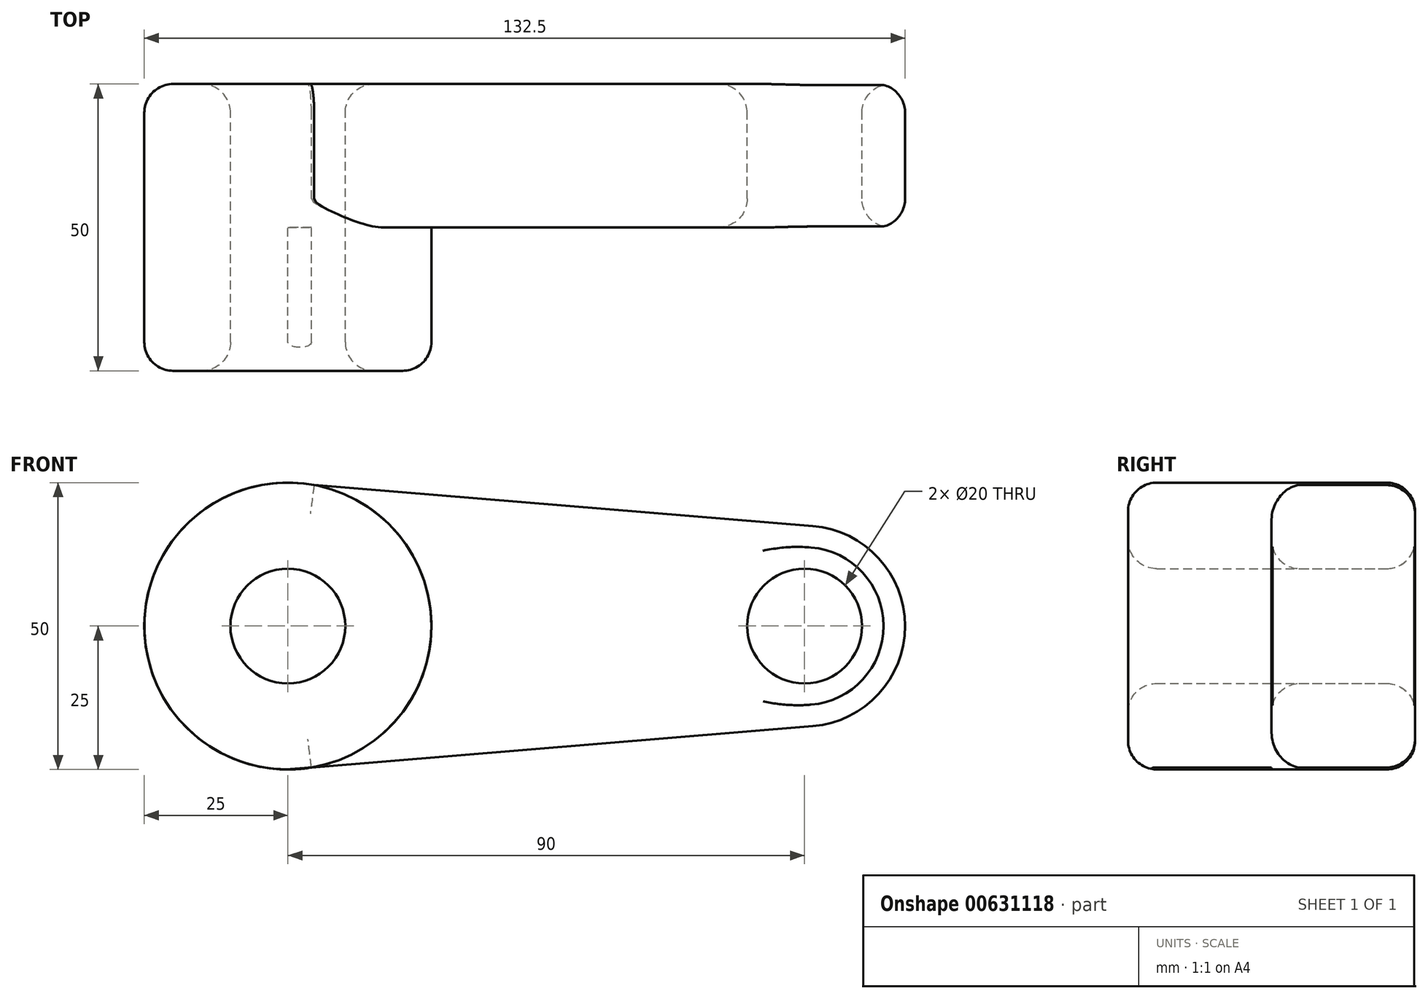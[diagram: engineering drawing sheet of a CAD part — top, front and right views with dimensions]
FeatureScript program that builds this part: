
annotation { "Feature Type Name" : "Feature", "Feature Type Description" : "" }
export const myFeature = defineFeature(function(context is Context, id is Id, definition is map)
    precondition{}
    {
        {
            var Q0;
            Q0=qCreatedBy(makeId("Front.planeOp"),FACE);
            var sketch = newSketch(context, id + "F0", { "sketchPlane" : qUnion([Q0])});
            skCircle(sketch, "E0", {"center": v(0, 0) * mm, "radius": 25 * mm});
            skCircle(sketch, "E1", {"center": v(90, 0) * mm, "radius": 17.5 * mm});
            skLineSegment(sketch, "E2", {"start": v(4.58, 24.58) * mm, "end": v(91.43, 17.44) * mm});
            skLineSegment(sketch, "E3", {"start": v(0, -25) * mm, "end": v(91.44, -17.44) * mm});
            skCircle(sketch, "E4", {"center": v(0, 0) * mm, "radius": 10 * mm});
            skCircle(sketch, "E5", {"center": v(90, 0) * mm, "radius": 10 * mm});
            skSolve(sketch);
        }
        {
            var Q0;
            Q0 = qSketchRegion(id + "F0", true);
            var Q1;
            Q1=makeQuery(id+"F0.imprint","IMPRINT",FACE,{"disambiguationData":[TD([[makeQuery(id+"F0.imprint","IMPRINT",EDGE,{"derivedFrom":sQuery(id+"F0.wireOp",EDGE,"E5")}),-1.0]])]});
            var Q2;
            Q2=makeQuery(id+"F0.imprint","IMPRINT",FACE,{"disambiguationData":[TD([[makeQuery(id+"F0.imprint","IMPRINT",EDGE,{"derivedFrom":sQuery(id+"F0.wireOp",EDGE,"E4")}),-1.0]])]});
            extrude(context, id + "F1", {"entities" : qUnion([Q0, Q1, Q2]), "depth" : 25 * mm, "offsetDistance" : 25 * mm});
        }
        {
            var Q0;
            Q0=makeQuery(id+"F0.imprint","IMPRINT",FACE,{"disambiguationData":[TD([[makeQuery(id+"F0.imprint","IMPRINT",EDGE,{"derivedFrom":sQuery(id+"F0.wireOp",EDGE,"E4")}),-1.0]])]});
            extrude(context, id + "F2", {"entities" : qUnion([Q0]), "operationType" : NewBodyOperationType.ADD, "depth" : 50 * mm, "offsetDistance" : 25 * mm});
        }
        {
            var Q0;
            {var subQ0=sQuery(id+"F0.wireOp",EDGE,"E4");Q0=makeQuery(id+"F2.boolean.opBoolean","MERGE",FACE,{"derivedFrom":[makeQuery(id+"F1.opExtrude","SWEPT_FACE",FACE,{"disambiguationData":[OSD([subQ0])]}),makeQuery(id+"F2.opExtrude","SWEPT_FACE",FACE,{"disambiguationData":[OSD([subQ0])]})]});}
            var Q1;
            Q1=makeQuery(id+"F2.opExtrude","CAP_EDGE",EDGE,{"disambiguationData":[OSD([sQuery(id+"F0.wireOp",EDGE,"E0")])],"isStart":false});
            var Q2;
            Q2=makeQuery(id+"F1.opExtrude","CAP_EDGE",EDGE,{"disambiguationData":[OSD([sQuery(id+"F0.wireOp",EDGE,"E3")])],"isStart":false});
            var Q3;
            Q3=makeQuery(id+"F1.opExtrude","CAP_EDGE",EDGE,{"disambiguationData":[OSD([sQuery(id+"F0.wireOp",EDGE,"E5")])],"isStart":false});
            var Q4;
            Q4=makeQuery(id+"F1.opExtrude","CAP_EDGE",EDGE,{"disambiguationData":[OSD([sQuery(id+"F0.wireOp",EDGE,"E1")])],"isStart":true});
            var Q5;
            Q5=makeQuery(id+"F1.opExtrude","SWEPT_FACE",FACE,{"disambiguationData":[OSD([sQuery(id+"F0.wireOp",EDGE,"E5")])]});
            var Q6;
            Q6=makeQuery(id+"F1.opExtrude","CAP_EDGE",EDGE,{"disambiguationData":[OSD([sQuery(id+"F0.wireOp",EDGE,"E3")])],"isStart":true});
            var Q7;
            Q7=makeQuery(id+"F1.opExtrude","CAP_EDGE",EDGE,{"disambiguationData":[OSD([sQuery(id+"F0.wireOp",EDGE,"E0")])],"isStart":true});
            fillet(context, id + "F3", {"entities" : qUnion([Q0, Q1, Q2, Q3, Q4, Q5, Q6, Q7]), "radius" : 5 * mm, "tangentPropagation" : true, "allowEdgeOverflow" : false});
        }
    });
